# Revit family: Gleitlager T HV1, o.D., Ø64 bis Ø219mm (h=100mm bis 126mm)
name_source: partatom
category: HLS-Bauteile
revit_build: Autodesk Revit 2018 (Build: 20190510_1515(x64)
units: mm (PartAtom-declared; Revit-internal decimal feet)

## family parameters
Arbeitsebenenbasiert = Ja
Beim Laden mit Abzugskörper schneiden = Nein
Bemaßung runder Anschluss = Durchmesser verwenden
Gemeinsam genutzt = Ja
Immer vertikal = Nein
Klassifizierung = Keine
Raumberechnungspunkt = Nein
Teiletyp = Normal

## types (13) — shared parameters
Anzahl Rohrschellen = 2
Breite Schellenband = 50 mm
Breite Unterbau = 100 mm
Fabrikat = MEFA
Firma = MEFA Befestigungs- und Montagesysteme GmbH
Hersteller = MEFA
Kurztext1 = Gleitlager T 2 RS HV1 50x5
Länge Unterbau = 250 mm
Mengeneinheit = St
Schalldämmeinlage = ohne Dämmung
Sicherheitsfaktor = 1.54
Stärke Material = 8 mm  [stored 0.0262467 ft]
Stärke Schellenband = 5 mm
Verschluss = Mutter / Verschluss-Schraube
Vorgabe-Ansicht = 1219 mm
max. Höhe Unterbau = 125 mm
min. Höhe Unterbau = 100 mm
vpe = 1
zero-valued in all types: Dämmstärke, max. Rohraußendurchmesser, min. Rohraußendurchmesser

## per-type parameters (varying)
| type | Artikelnummer | EAN | Gewicht | Gewicht pro Bauteil | Kurztext2 | Schellenteil | max. Rohrachse | min. Rohrachse |
| Typ HV1, m. 2 RS, o.D., Ø64mm (h=100 bis 126mm) | 141afba0064 | 4250928460349 | 4.88 kg | 4.88 kg | 64 mm o. Dämm. 100x250 mm fsv | TL-141S_b0064 bis 0219, o.D : mit RS Ø64mm o.D | 158 mm | 132 mm |
| Typ HV1, m. 2 RS, o.D., Ø76mm (h=100 bis 126mm) | 141afba0076 | 4250928460356 | 5.08 kg | 5.08 kg | 76 mm o. Dämm. 100x250 mm fsv | TL-141S_b0064 bis 0219, o.D : mit RS Ø76mm o.D | 164 mm | 138 mm |
| Typ HV1, m. 2 RS, o.D., Ø89mm (h=100 bis 126mm) | 141afba0089 | 4250928460363 | 5.23 kg | 5.23 kg | 89 mm o. Dämm. 100x250 mm fsv | TL-141S_b0064 bis 0219, o.D : mit RS Ø88.9mm, o.D | 171 mm | 145 mm |
| Typ HV1, m. 2 RS, o.D., Ø108mm (h=100 bis 126mm) | 141afba0108 | 4250928460370 | 5.49 kg | 5.49 kg | 108 mm o. Dämm. 100x250 mm fsv | TL-141S_b0064 bis 0219, o.D : mit RS Ø108mm o.D | 180 mm | 154 mm |
| Typ HV1, m. 2 RS, o.D., Ø110mm (h=100 bis 126mm) | 141afba0110 | 4250928460387 | 5.52 kg | 5.52 kg | 110 mm o. Dämm. 100x250 mm fsv | TL-141S_b0064 bis 0219, o.D : mit RS Ø110mm o.D | 181 mm | 155 mm |
| Typ HV1, m. 2 RS, o.D., Ø133mm (h=100 bis 126mm) | 141afba0133 | 4250928460400 | 5.84 kg | 5.84 kg | 133 mm o. Dämm. 100x250 mm fsv | TL-141S_b0064 bis 0219, o.D : mit RS Ø133mm o.D | 193 mm | 167 mm |
| Typ HV1, m. 2 RS, o.D., Ø114mm (h=100 bis 126mm) | 141afba0114 | 4250928460394 | 5.57 kg | 5.57 kg | 114 mm o. Dämm. 100x250 mm fsv | TL-141S_b0114, o.D : mit RS Ø114mm o.D | 183 mm | 157 mm |
| Typ HV1, m. 2 RS, o.D., Ø140mm (h=100 bis 126mm) | 141afba0140 | 4250928460417 | 5.93 kg | 5.93 kg | 140 mm o. Dämm. 100x250 mm fsv | TL-141S_b0064 bis 0219, o.D : mit RS Ø139.7mm o.D | 196 mm | 170 mm |
| Typ HV1, m. 2 RS, o.D., Ø160mm (h=100 bis 126mm) | 141afba0160 | 4250928460424 | 6.22 kg | 6.22 kg | 160 mm o. Dämm. 100x250 mm fsv | TL-141S_b0064 bis 0219, o.D : mit RS Ø160mm o.D | 206 mm | 180 mm |
| Typ HV1, m. 2 RS, o.D., Ø168mm (h=100 bis 126mm) | 141afba0168 | 4250928460431 | 6.33 kg | 6.33 kg | 168 mm o. Dämm. 100x250 mm fsv | TL-141S_b0064 bis 0219, o.D : mit RS Ø168.3mm o.D | 210 mm | 184 mm |
| Typ HV1, m. 2 RS, o.D., Ø180mm (h=100 bis 126mm) | 141afba0180 | 4250928460448 | 6.50 kg | 6.50 kg | 180 mm o. Dämm. 100x250 mm fsv | TL-141S_b0064 bis 0219, o.D : mit RS Ø180mm o.D | 216 mm | 190 mm |
| Typ HV1, m. 2 RS, o.D., Ø210mm (h=100 bis 126mm) | 141afba0210 | 4250928460455 | 6.91 kg | 6.91 kg | 210 mm o. Dämm. 100x250 mm fsv | TL-141S_b0064 bis 0219, o.D : mit RS Ø210mm o.D | 231 mm | 205 mm |
| Typ HV1, m. 2 RS, o.D., Ø219mm (h=100 bis 126mm) | 141afba0219 | 4250928460462 | 7.04 kg | 7.04 kg | 219 mm o. Dämm. 100x250 mm fsv | TL-141S_b0064 bis 0219, o.D : mit RS Ø219mm o.D | 236 mm | 210 mm |

note: [stored X ft] marks values corroborated as IEEE doubles in the binary element streams (Revit-internal decimal feet)

## geometry (parser evidence)
native form markers: Sweep x19
no freeform markers — native parametric forms only
